# Revit family: FXL - Yoke
name_source: partatom
category: Lighting Fixtures
units: mm (PartAtom-declared; Revit-internal decimal feet)

## family parameters
Cut with Voids When Loaded = No
Host = Face
Light Source = No
OmniClass Number = 23.80.70.14.14
OmniClass Title = Exterior Floodlights
Part Type = Normal
Room Calculation Point = No
Round Connector Dimension = Use Diameter
Shared = Yes

## types (1)
- FXL Yoke - RD
    Apparent Load = 0 VA
    Default Elevation = 48.000"
    Description = Office buildings, monuments, facades, columns, flag poles, bridges, commercial, mixed retail, apartments, schools and campuse
    Finish = Red
    Lens = White Glass
    Manufacturer = EXO
    Model = FXL 84 LED Floodlight
    Photometric Web = Web ARF4 - Yoke : ARF4-X-84L3K-700-M-U
    Pivot Angle = 0.00°
    Pivot calc. = 90.00°
    Stand = Red
    Tilt Angle = 0.00°
    Total Input Wattage = 194 W
    URL = https://www.currentlighting.com
    Voltage = 120 V

## geometry (parser evidence)
native form markers: Blend x10, Sweep x6
no freeform markers — native parametric forms only
